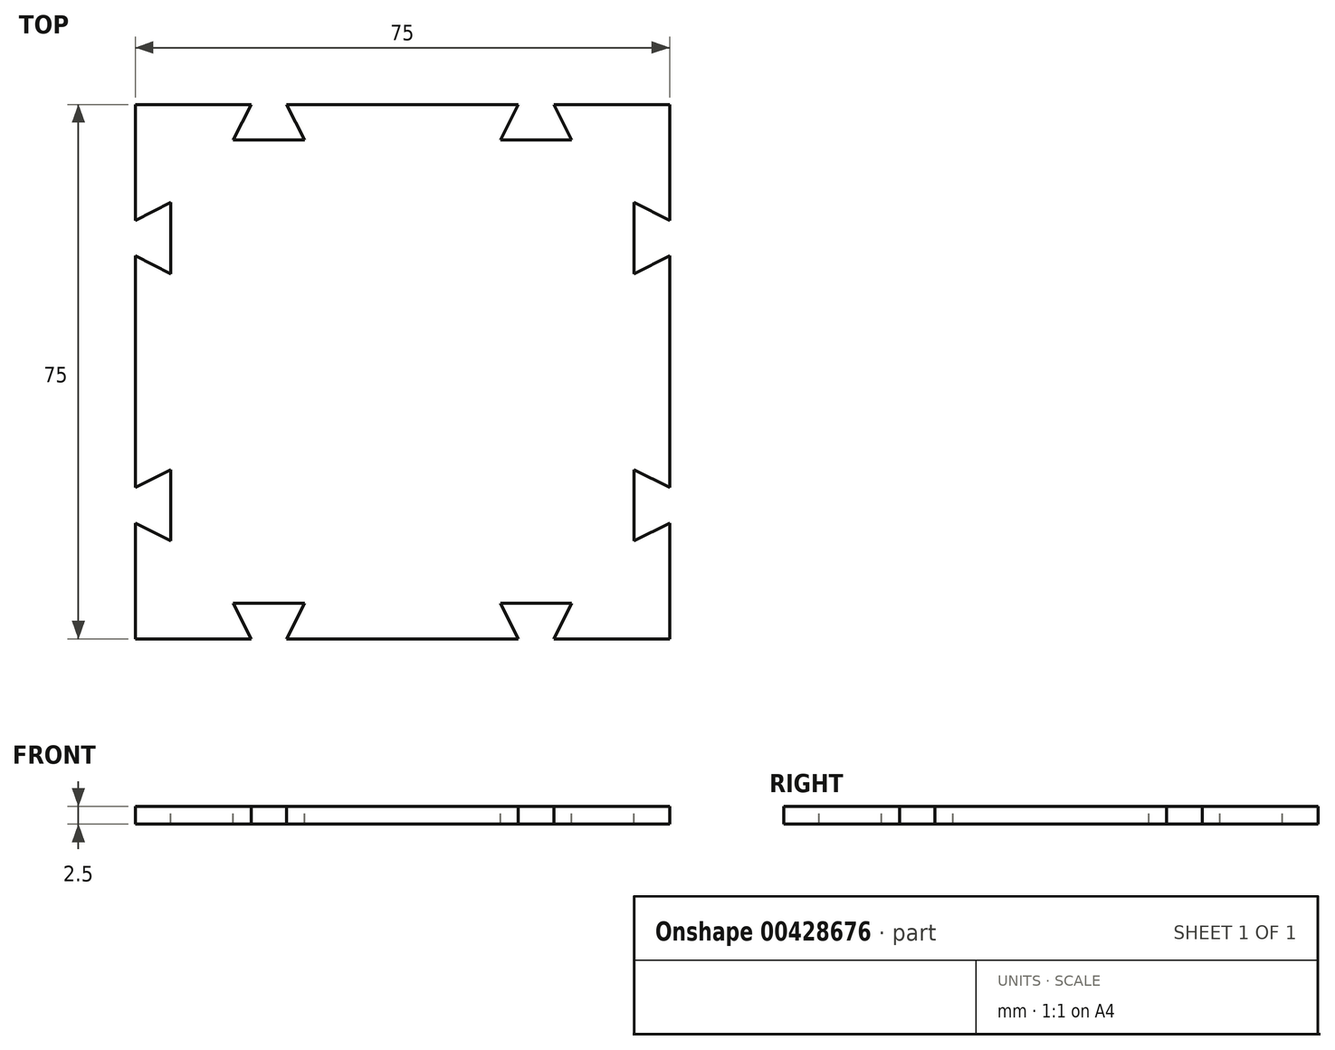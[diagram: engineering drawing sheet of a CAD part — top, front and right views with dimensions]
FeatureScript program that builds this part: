
annotation { "Feature Type Name" : "Feature", "Feature Type Description" : "" }
export const myFeature = defineFeature(function(context is Context, id is Id, definition is map)
    precondition{}
    {
        {
            var Q0;
            Q0=qCreatedBy(makeId("Top.planeOp"),FACE);
            var sketch = newSketch(context, id + "F0", { "sketchPlane" : qUnion([Q0])});
            skLineSegment(sketch, "E0.bottom", {"start": v(-37.5, 37.5) * mm, "end": v(37.5, 37.5) * mm});
            skLineSegment(sketch, "E0.top", {"start": v(-37.5, -37.5) * mm, "end": v(37.5, -37.5) * mm});
            skLineSegment(sketch, "E0.left", {"start": v(-37.5, 37.5) * mm, "end": v(-37.5, -37.5) * mm});
            skLineSegment(sketch, "E0.right", {"start": v(37.5, 37.5) * mm, "end": v(37.5, -37.5) * mm});
            skSolve(sketch);
        }
        {
            var Q0;
            Q0=makeQuery(id+"F0.imprint","IMPRINT",FACE,{"disambiguationData":[TD([[makeQuery(id+"F0.imprint","IMPRINT",EDGE,{"derivedFrom":sQuery(id+"F0.wireOp",EDGE,"E0.bottom")}),-1.0]])]});
            extrude(context, id + "F1", {"entities" : qUnion([Q0]), "oppositeDirection" : true, "depth" : 2.5 * mm});
        }
        {
            var Q0;
            Q0=qCreatedBy(makeId("Top.planeOp"),FACE);
            var sketch = newSketch(context, id + "F2", { "sketchPlane" : qUnion([Q0])});
            skLineSegment(sketch, "E1.left", {"start": v(-32.5, 23.75) * mm, "end": v(-32.5, 13.75) * mm});
            skLineSegment(sketch, "E1.right", {"start": v(-37.5, 21.25) * mm, "end": v(-37.5, 16.25) * mm});
            skLineSegment(sketch, "E2", {"start": v(-37.5, 21.25) * mm, "end": v(-32.5, 23.75) * mm});
            skLineSegment(sketch, "E3", {"start": v(-37.5, 16.25) * mm, "end": v(-32.5, 13.75) * mm});
            skPoint(sketch, "E4", {"position": v(-37.5, 18.75) * mm});
            skPoint(sketch, "E5", {"position": v(-32.5, 18.75) * mm});
            skLineSegment(sketch, "E6.MirrorCS", {"start": v(-37.5, -16.25) * mm, "end": v(-32.5, -13.75) * mm});
            skLineSegment(sketch, "E7.MirrorCS", {"start": v(-32.5, -23.75) * mm, "end": v(-32.5, -13.75) * mm});
            skLineSegment(sketch, "E8.MirrorCS", {"start": v(-37.5, -21.25) * mm, "end": v(-32.5, -23.75) * mm});
            skLineSegment(sketch, "E9.MirrorCS", {"start": v(-37.5, -21.25) * mm, "end": v(-37.5, -16.25) * mm});
            skLineSegment(sketch, "E10.MirrorCS", {"start": v(32.5, 23.75) * mm, "end": v(32.5, 13.75) * mm});
            skLineSegment(sketch, "E11.MirrorCS", {"start": v(37.5, 21.25) * mm, "end": v(32.5, 23.75) * mm});
            skPoint(sketch, "E12.MirrorP", {"position": v(37.5, 18.75) * mm});
            skLineSegment(sketch, "E13.MirrorCS", {"start": v(37.5, 16.25) * mm, "end": v(32.5, 13.75) * mm});
            skLineSegment(sketch, "E14.MirrorCS", {"start": v(37.5, 21.25) * mm, "end": v(37.5, 16.25) * mm});
            skLineSegment(sketch, "E15.MirrorCS", {"start": v(32.5, -23.75) * mm, "end": v(32.5, -13.75) * mm});
            skLineSegment(sketch, "E16.MirrorCS", {"start": v(37.5, -16.25) * mm, "end": v(32.5, -13.75) * mm});
            skLineSegment(sketch, "E17.MirrorCS", {"start": v(37.5, -21.25) * mm, "end": v(37.5, -16.25) * mm});
            skLineSegment(sketch, "E18.MirrorCS", {"start": v(37.5, -21.25) * mm, "end": v(32.5, -23.75) * mm});
            skLineSegment(sketch, "E19.bottom", {"start": v(-21.25, 37.5) * mm, "end": v(-16.25, 37.5) * mm});
            skLineSegment(sketch, "E19.top", {"start": v(-23.75, 32.5) * mm, "end": v(-13.75, 32.5) * mm});
            skLineSegment(sketch, "E20", {"start": v(-23.75, 32.5) * mm, "end": v(-21.25, 37.5) * mm});
            skLineSegment(sketch, "E21", {"start": v(-16.25, 37.5) * mm, "end": v(-13.75, 32.5) * mm});
            skPoint(sketch, "E22", {"position": v(-18.75, 37.5) * mm});
            skPoint(sketch, "E23", {"position": v(-18.75, 32.5) * mm});
            skLineSegment(sketch, "E24.MirrorCS", {"start": v(16.25, 37.5) * mm, "end": v(13.75, 32.5) * mm});
            skLineSegment(sketch, "E25.MirrorCS", {"start": v(23.75, 32.5) * mm, "end": v(13.75, 32.5) * mm});
            skPoint(sketch, "E26.MirrorP", {"position": v(18.75, 37.5) * mm});
            skLineSegment(sketch, "E27.MirrorCS", {"start": v(21.25, 37.5) * mm, "end": v(16.25, 37.5) * mm});
            skLineSegment(sketch, "E28.MirrorCS", {"start": v(23.75, 32.5) * mm, "end": v(21.25, 37.5) * mm});
            skLineSegment(sketch, "E29.MirrorCS", {"start": v(-23.75, -32.5) * mm, "end": v(-13.75, -32.5) * mm});
            skLineSegment(sketch, "E30.MirrorCS", {"start": v(-23.75, -32.5) * mm, "end": v(-21.25, -37.5) * mm});
            skLineSegment(sketch, "E31.MirrorCS", {"start": v(-21.25, -37.5) * mm, "end": v(-16.25, -37.5) * mm});
            skLineSegment(sketch, "E32.MirrorCS", {"start": v(-16.25, -37.5) * mm, "end": v(-13.75, -32.5) * mm});
            skLineSegment(sketch, "E33.MirrorCS", {"start": v(21.25, -37.5) * mm, "end": v(16.25, -37.5) * mm});
            skLineSegment(sketch, "E34.MirrorCS", {"start": v(23.75, -32.5) * mm, "end": v(21.25, -37.5) * mm});
            skLineSegment(sketch, "E35.MirrorCS", {"start": v(23.75, -32.5) * mm, "end": v(13.75, -32.5) * mm});
            skLineSegment(sketch, "E36.MirrorCS", {"start": v(16.25, -37.5) * mm, "end": v(13.75, -32.5) * mm});
            skSolve(sketch);
        }
        {
            var Q0;
            Q0 = qSketchRegion(id + "F2", true);
            extrude(context, id + "F3", {"entities" : qUnion([Q0]), "operationType" : NewBodyOperationType.REMOVE, "endBound" : BoundingType.UP_TO_NEXT, "oppositeDirection" : true, "depth" : 25 * mm});
        }
    });
